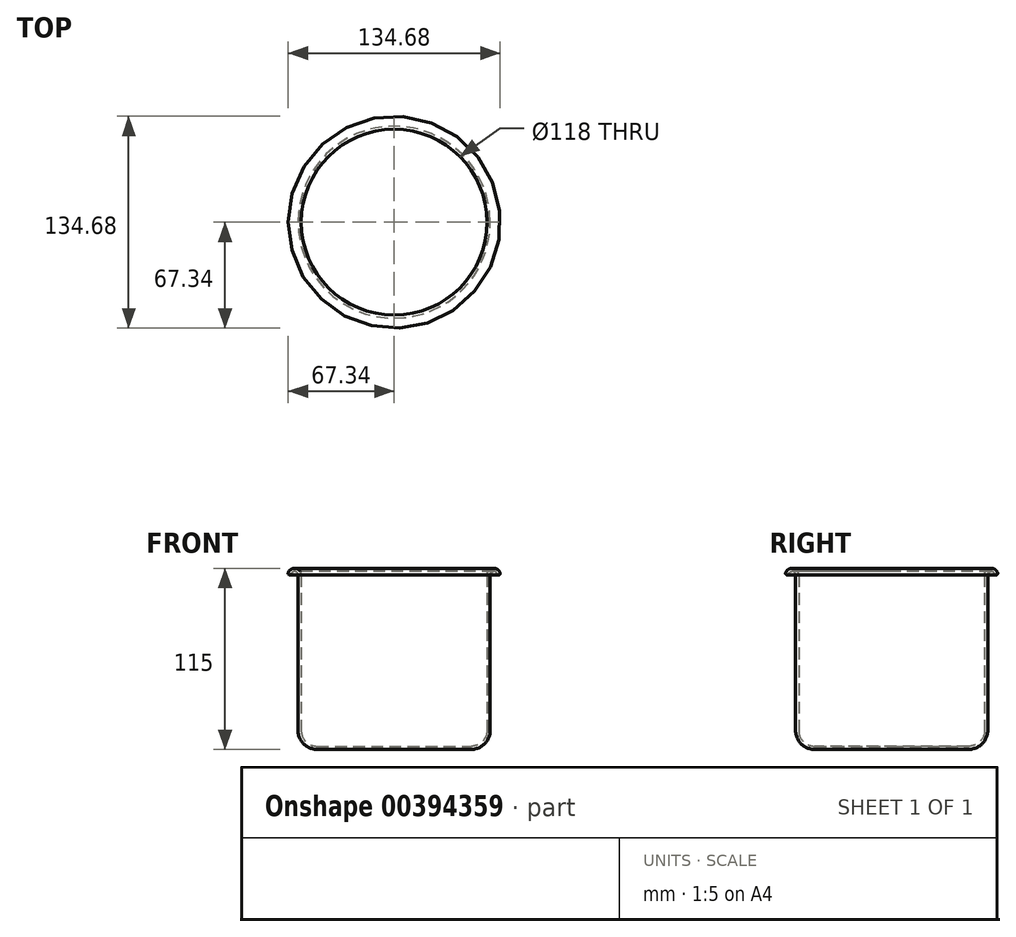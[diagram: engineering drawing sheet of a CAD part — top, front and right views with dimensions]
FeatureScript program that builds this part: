
annotation { "Feature Type Name" : "Feature", "Feature Type Description" : "" }
export const myFeature = defineFeature(function(context is Context, id is Id, definition is map)
    precondition{}
    {
        {
            var Q0;
            Q0=qCreatedBy(makeId("Front.planeOp"),FACE);
            var sketch = newSketch(context, id + "F0", { "sketchPlane" : qUnion([Q0])});
            skLineSegment(sketch, "E0", {"start": v(0, 0) * mm, "end": v(0, 99.86) * mm});
            skLineSegment(sketch, "E1.bottom", {"start": v(59, 110.75) * mm, "end": v(61, 110.75) * mm});
            skLineSegment(sketch, "E1.left", {"start": v(59, 110.75) * mm, "end": v(59, 12) * mm});
            skLineSegment(sketch, "E2.bottom", {"start": v(49, 2) * mm, "end": v(0, 2) * mm});
            skLineSegment(sketch, "E2.right", {"start": v(0, 2) * mm, "end": v(0, 0) * mm});
            skArc(sketch, "E3", {"start": v(67.3, 112.06) * mm, "mid": v(62.59, 114.95) * mm, "end": v(59, 110.75) * mm});
            skLineSegment(sketch, "E4", {"start": v(63.25, 115) * mm, "end": v(85.42, 115) * mm, "construction": true});
            skLineSegment(sketch, "E5", {"start": v(0, 0) * mm, "end": v(49, 0) * mm});
            skLineSegment(sketch, "E6", {"start": v(61, 12) * mm, "end": v(61, 93.99) * mm});
            skPoint(sketch, "E7.visualSharp", {"position": v(59, 2) * mm});
            skArc(sketch, "E7.filletArc", {"start": v(49, 2) * mm, "mid": v(56.07, 4.93) * mm, "end": v(59, 12) * mm});
            skPoint(sketch, "E8.visualSharp", {"position": v(61, 0) * mm});
            skArc(sketch, "E8.filletArc", {"start": v(49, 0) * mm, "mid": v(57.49, 3.51) * mm, "end": v(61, 12) * mm});
            skLineSegment(sketch, "E9", {"start": v(61, 93.99) * mm, "end": v(61, 110.75) * mm});
            skArc(sketch, "E10", {"start": v(65.4, 111.44) * mm, "mid": v(62.9, 112.97) * mm, "end": v(61, 110.75) * mm});
            skLineSegment(sketch, "E11.trimOffspring", {"start": v(66.34, 110.75) * mm, "end": v(66.34, 110.75) * mm});
            skPoint(sketch, "E12.visualSharp", {"position": v(67.5, 110.75) * mm});
            skArc(sketch, "E12.filletArc", {"start": v(66.34, 110.75) * mm, "mid": v(67.15, 111.16) * mm, "end": v(67.3, 112.06) * mm});
            skPoint(sketch, "E13.visualSharp", {"position": v(65.5, 110.75) * mm});
            skArc(sketch, "E13.filletArc", {"start": v(65.4, 111.44) * mm, "mid": v(65.75, 110.94) * mm, "end": v(66.34, 110.75) * mm});
            skSolve(sketch);
        }
        {
            var Q0;
            Q0=makeQuery(id+"F0.imprint","IMPRINT",FACE,{"disambiguationData":[TD([[makeQuery(id+"F0.imprint","IMPRINT",EDGE,{"derivedFrom":sQuery(id+"F0.wireOp",EDGE,"E1.bottom")}),-1.0]])]});
            var Q1;
            Q1=makeQuery(id+"F0.imprint","IMPRINT",FACE,{"disambiguationData":[TD([[makeQuery(id+"F0.imprint","IMPRINT",EDGE,{"derivedFrom":sQuery(id+"F0.wireOp",EDGE,"E1.bottom")}),1.0]])]});
            var Q2;
            Q2=sQuery(id+"F0.wireOp",EDGE,"E0");
            revolve(context, id + "F1", {"entities" : qUnion([Q0, Q1]), "axis" : qUnion([Q2]), "revolveType" : RevolveType.FULL});
        }
    });
